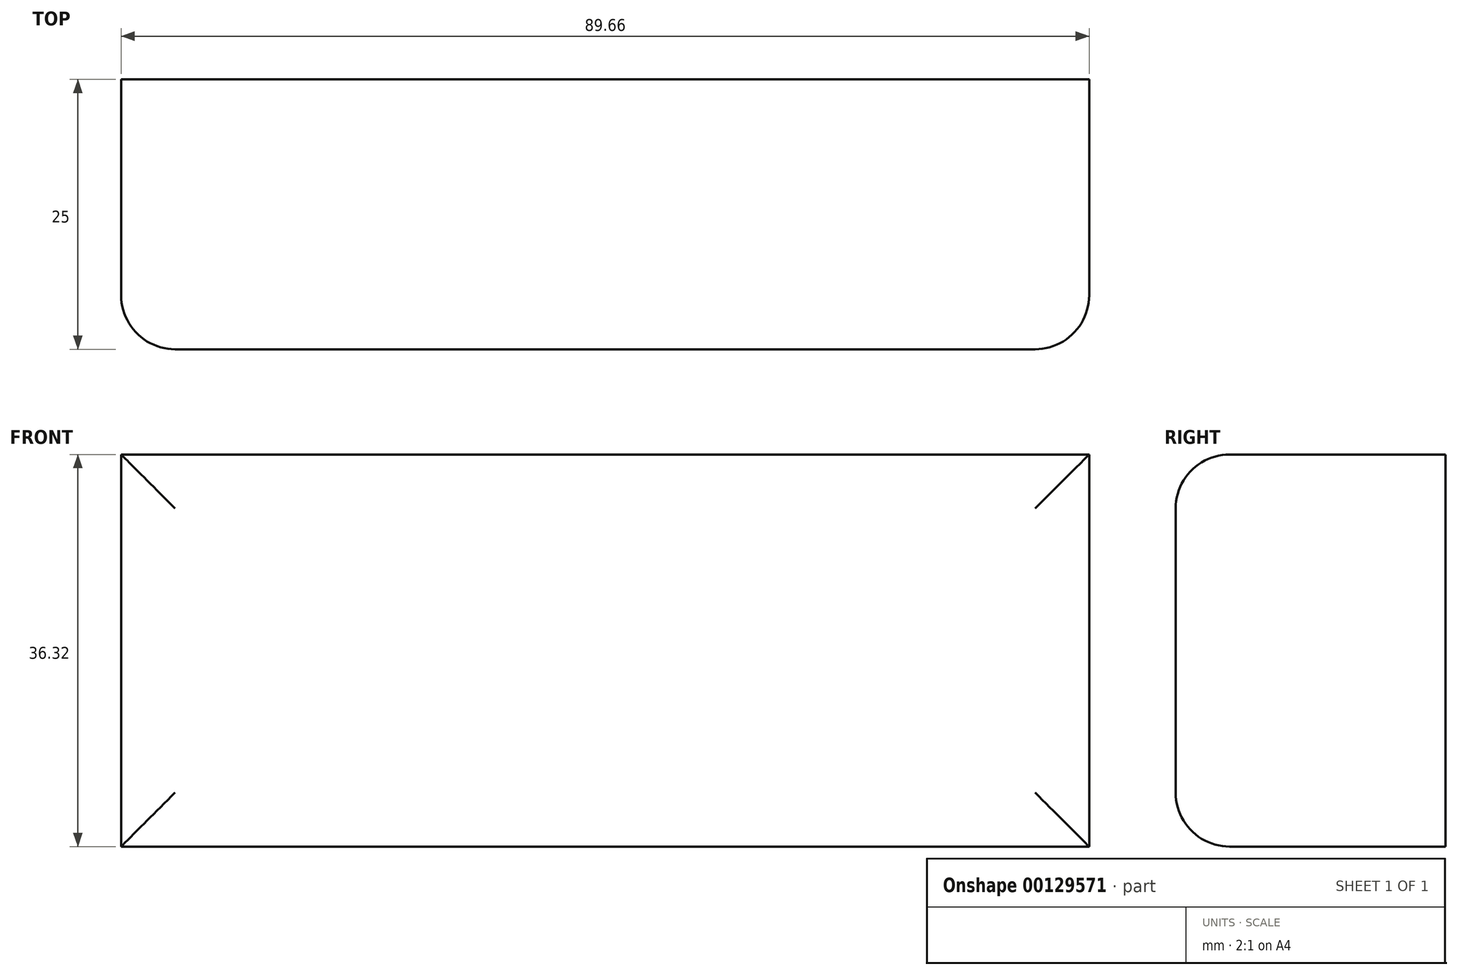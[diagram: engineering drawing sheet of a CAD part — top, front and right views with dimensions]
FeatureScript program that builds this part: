
annotation { "Feature Type Name" : "Feature", "Feature Type Description" : "" }
export const myFeature = defineFeature(function(context is Context, id is Id, definition is map)
    precondition{}
    {
        {
            var Q0;
            Q0=qCreatedBy(makeId("Front.planeOp"),FACE);
            var sketch = newSketch(context, id + "F0", { "sketchPlane" : qUnion([Q0])});
            skLineSegment(sketch, "E0", {"start": v(-42.03, 0) * mm, "end": v(47.03, 0) * mm});
            skLineSegment(sketch, "E1.bottom", {"start": v(-42.03, 0) * mm, "end": v(47.63, 0) * mm});
            skLineSegment(sketch, "E1.top", {"start": v(-42.03, 36.32) * mm, "end": v(47.63, 36.32) * mm});
            skLineSegment(sketch, "E1.left", {"start": v(-42.03, 0) * mm, "end": v(-42.03, 36.32) * mm});
            skLineSegment(sketch, "E1.right", {"start": v(47.63, 0) * mm, "end": v(47.63, 36.32) * mm});
            skSolve(sketch);
        }
        {
            var Q0;
            Q0=makeQuery(id+"F0.imprint","IMPRINT",FACE,{"disambiguationData":[TD([[makeQuery(id+"F0.imprint","IMPRINT",EDGE,{"derivedFrom":sQuery(id+"F0.wireOp",EDGE,"E1.top")}),-1.0]])]});
            extrude(context, id + "F1", {"entities" : qUnion([Q0]), "depth" : 25 * mm});
        }
        {
            var Q0;
            Q0=makeQuery(id+"F1.opExtrude","CAP_EDGE",EDGE,{"disambiguationData":[OSD([sQuery(id+"F0.wireOp",EDGE,"E1.left")])],"isStart":false});
            var Q1;
            Q1=makeQuery(id+"F1.opExtrude","CAP_EDGE",EDGE,{"disambiguationData":[OSD([sQuery(id+"F0.wireOp",EDGE,"E1.top")])],"isStart":false});
            var Q2;
            Q2=makeQuery(id+"F1.opExtrude","CAP_FACE",FACE,{"disambiguationData":[OSD([sQuery(id+"F0.wireOp",EDGE,"E1.bottom"),sQuery(id+"F0.wireOp",EDGE,"E1.top"),sQuery(id+"F0.wireOp",EDGE,"E1.left"),sQuery(id+"F0.wireOp",EDGE,"E1.right")])],"isStart":false});
            var Q3;
            Q3=makeQuery(id+"F1.opExtrude","CAP_EDGE",EDGE,{"disambiguationData":[OSD([sQuery(id+"F0.wireOp",EDGE,"E1.bottom")])],"isStart":false});
            fillet(context, id + "F2", {"entities" : qUnion([Q0, Q1, Q2, Q3]), "radius" : 5 * mm, "tangentPropagation" : true, "allowEdgeOverflow" : false});
        }
    });
